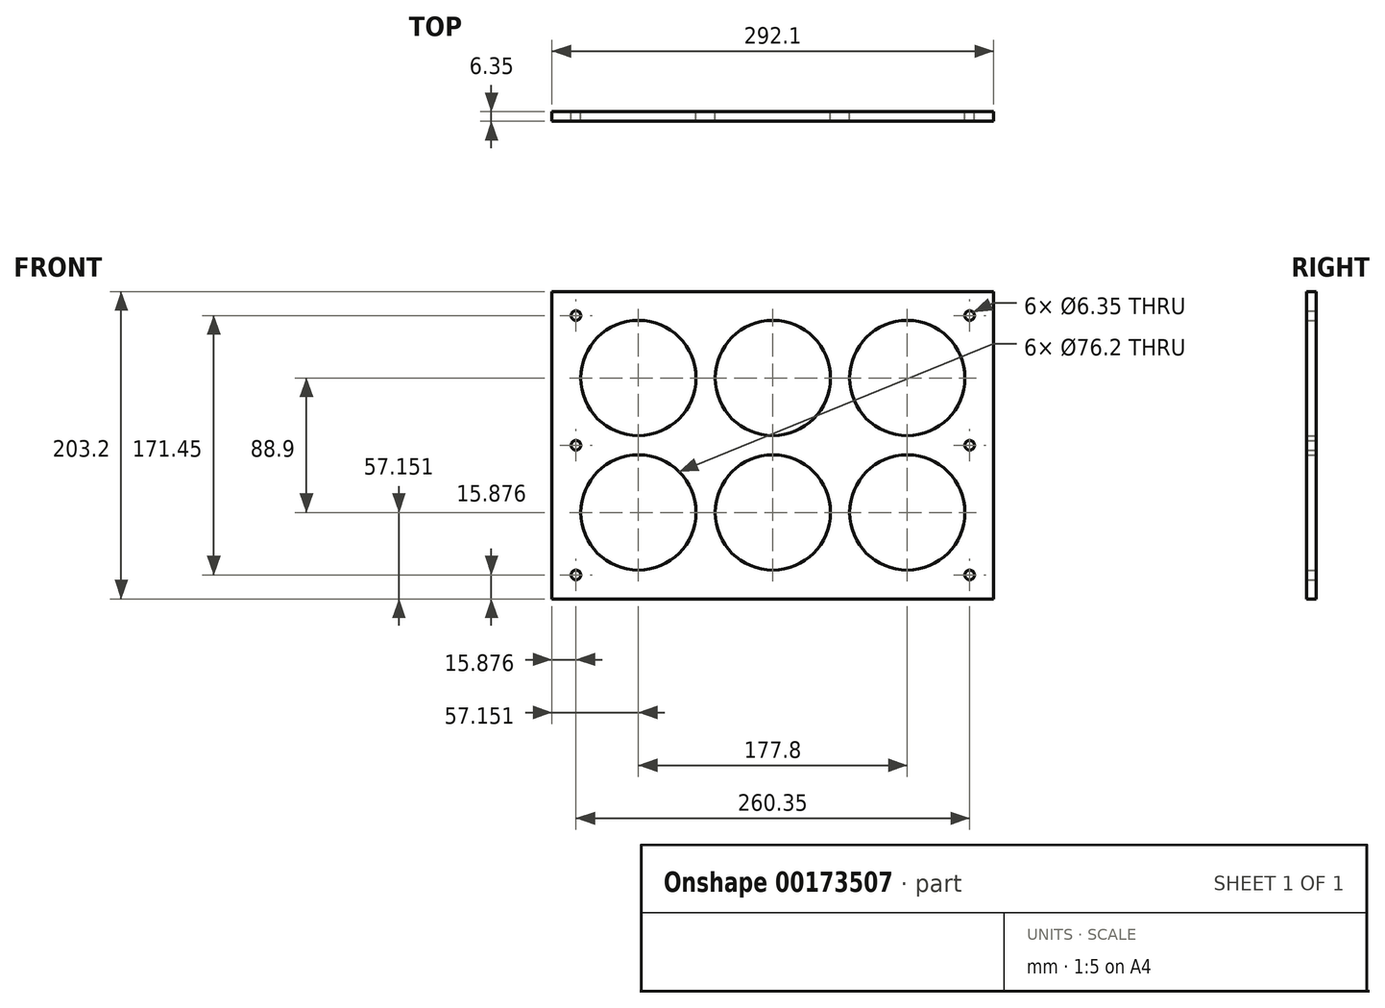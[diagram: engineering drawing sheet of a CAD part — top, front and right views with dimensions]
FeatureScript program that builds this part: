
annotation { "Feature Type Name" : "Feature", "Feature Type Description" : "" }
export const myFeature = defineFeature(function(context is Context, id is Id, definition is map)
    precondition{}
    {
        {
            var Q0;
            Q0=qCreatedBy(makeId("Front.planeOp"),FACE);
            var sketch = newSketch(context, id + "F0", { "sketchPlane" : qUnion([Q0])});
            skCircle(sketch, "E0", {"center": v(-52.94, 27.07) * mm, "radius": 38.1 * mm});
            skCircle(sketch, "E1.0.1.0", {"center": v(-52.94, 115.97) * mm, "radius": 38.1 * mm});
            skCircle(sketch, "E1.1.0.0", {"center": v(35.96, 27.07) * mm, "radius": 38.1 * mm});
            skCircle(sketch, "E1.1.1.0", {"center": v(35.96, 115.97) * mm, "radius": 38.1 * mm});
            skCircle(sketch, "E1.2.0.0", {"center": v(124.86, 27.07) * mm, "radius": 38.1 * mm});
            skCircle(sketch, "E1.2.1.0", {"center": v(124.86, 115.97) * mm, "radius": 38.1 * mm});
            skLineSegment(sketch, "E2", {"start": v(182.01, 173.12) * mm, "end": v(182.01, -30.08) * mm});
            skLineSegment(sketch, "E3", {"start": v(182.01, 173.12) * mm, "end": v(-110.09, 173.12) * mm});
            skLineSegment(sketch, "E4", {"start": v(-110.09, -30.08) * mm, "end": v(-110.09, 173.12) * mm});
            skLineSegment(sketch, "E5", {"start": v(-110.09, -30.08) * mm, "end": v(182.01, -30.08) * mm});
            skLineSegment(sketch, "E6.0", {"start": v(166.14, 157.25) * mm, "end": v(-94.21, 157.25) * mm, "construction": true});
            skLineSegment(sketch, "E6.1", {"start": v(166.14, 157.25) * mm, "end": v(166.14, -14.2) * mm, "construction": true});
            skLineSegment(sketch, "E6.2", {"start": v(-94.21, -14.2) * mm, "end": v(166.14, -14.2) * mm, "construction": true});
            skLineSegment(sketch, "E6.3", {"start": v(-94.21, -14.2) * mm, "end": v(-94.21, 157.25) * mm, "construction": true});
            skLineSegment(sketch, "E7", {"start": v(-94.21, 71.52) * mm, "end": v(166.14, 71.52) * mm, "construction": true});
            skCircle(sketch, "E8", {"center": v(-94.21, 157.25) * mm, "radius": 3.18 * mm});
            skCircle(sketch, "E9.0.1.0", {"center": v(-94.21, 71.52) * mm, "radius": 3.18 * mm});
            skCircle(sketch, "E9.0.2.0", {"center": v(-94.21, -14.2) * mm, "radius": 3.18 * mm});
            skCircle(sketch, "E9.1.0.0", {"center": v(166.14, 157.25) * mm, "radius": 3.18 * mm});
            skCircle(sketch, "E9.1.1.0", {"center": v(166.14, 71.52) * mm, "radius": 3.18 * mm});
            skCircle(sketch, "E9.1.2.0", {"center": v(166.14, -14.2) * mm, "radius": 3.18 * mm});
            skLineSegment(sketch, "E9.direction1", {"start": v(-94.21, 157.25) * mm, "end": v(166.14, 157.25) * mm, "construction": true});
            skLineSegment(sketch, "E9.direction2", {"start": v(-94.21, 157.25) * mm, "end": v(-94.21, 71.52) * mm, "construction": true});
            skSolve(sketch);
        }
        {
            var Q0;
            Q0=makeQuery(id+"F0.imprint","IMPRINT",FACE,{"disambiguationData":[TD([[makeQuery(id+"F0.imprint","IMPRINT",EDGE,{"derivedFrom":sQuery(id+"F0.wireOp",EDGE,"E0")}),-1.0]])]});
            extrude(context, id + "F1", {"entities" : qUnion([Q0]), "depth" : 6.35 * mm});
        }
    });
